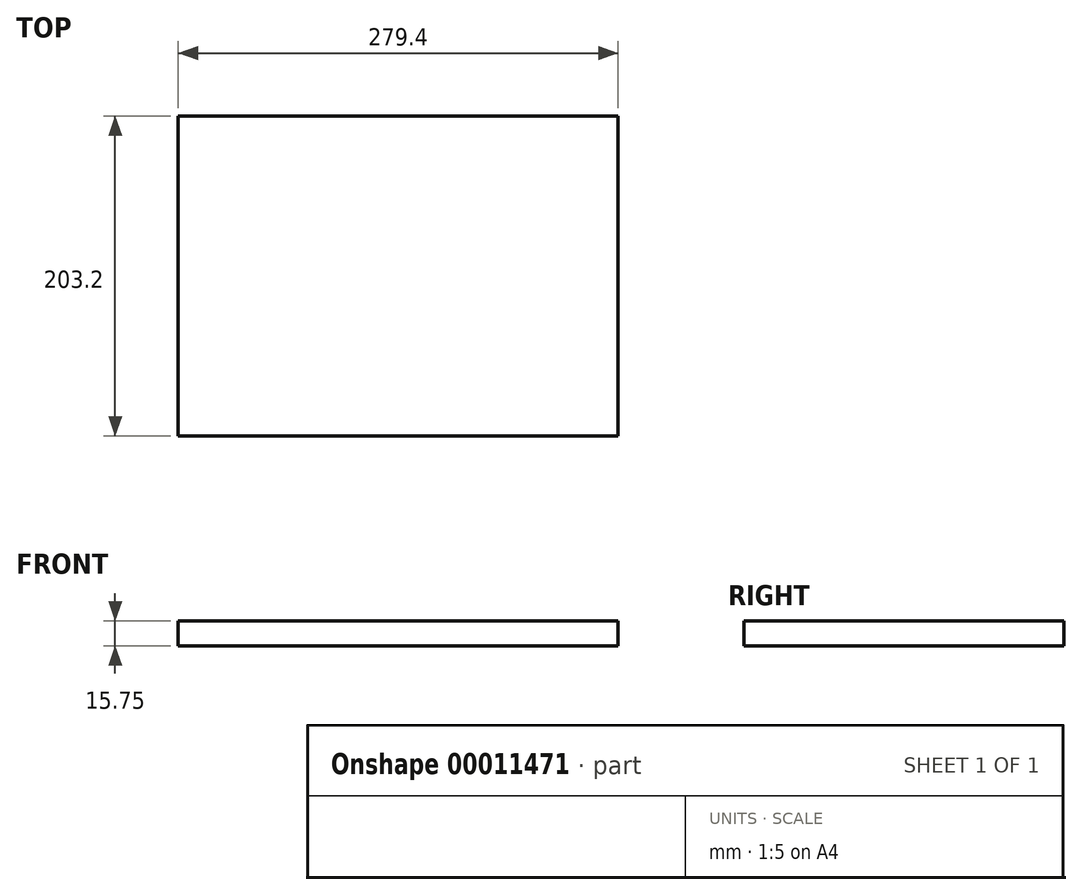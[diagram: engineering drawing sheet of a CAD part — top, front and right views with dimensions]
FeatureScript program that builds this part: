
annotation { "Feature Type Name" : "Feature", "Feature Type Description" : "" }
export const myFeature = defineFeature(function(context is Context, id is Id, definition is map)
    precondition{}
    {
        {
            var Q0;
            Q0=qCreatedBy(makeId("Top.planeOp"),FACE);
            var sketch = newSketch(context, id + "F0", { "sketchPlane" : qUnion([Q0])});
            skLineSegment(sketch, "E0.bottom", {"start": v(-139.7, 101.6) * mm, "end": v(139.7, 101.6) * mm});
            skLineSegment(sketch, "E0.top", {"start": v(-139.7, -101.6) * mm, "end": v(139.7, -101.6) * mm});
            skLineSegment(sketch, "E0.left", {"start": v(-139.7, 101.6) * mm, "end": v(-139.7, -101.6) * mm});
            skLineSegment(sketch, "E0.right", {"start": v(139.7, 101.6) * mm, "end": v(139.7, -101.6) * mm});
            skSolve(sketch);
        }
        {
            var Q0;
            Q0=makeQuery(id+"F0.imprint","IMPRINT",FACE,{"disambiguationData":[TD([[makeQuery(id+"F0.imprint","IMPRINT",EDGE,{"derivedFrom":sQuery(id+"F0.wireOp",EDGE,"E0.bottom")}),-1.0]])]});
            extrude(context, id + "F1", {"entities" : qUnion([Q0]), "depth" : 15.75 * mm});
        }
    });
